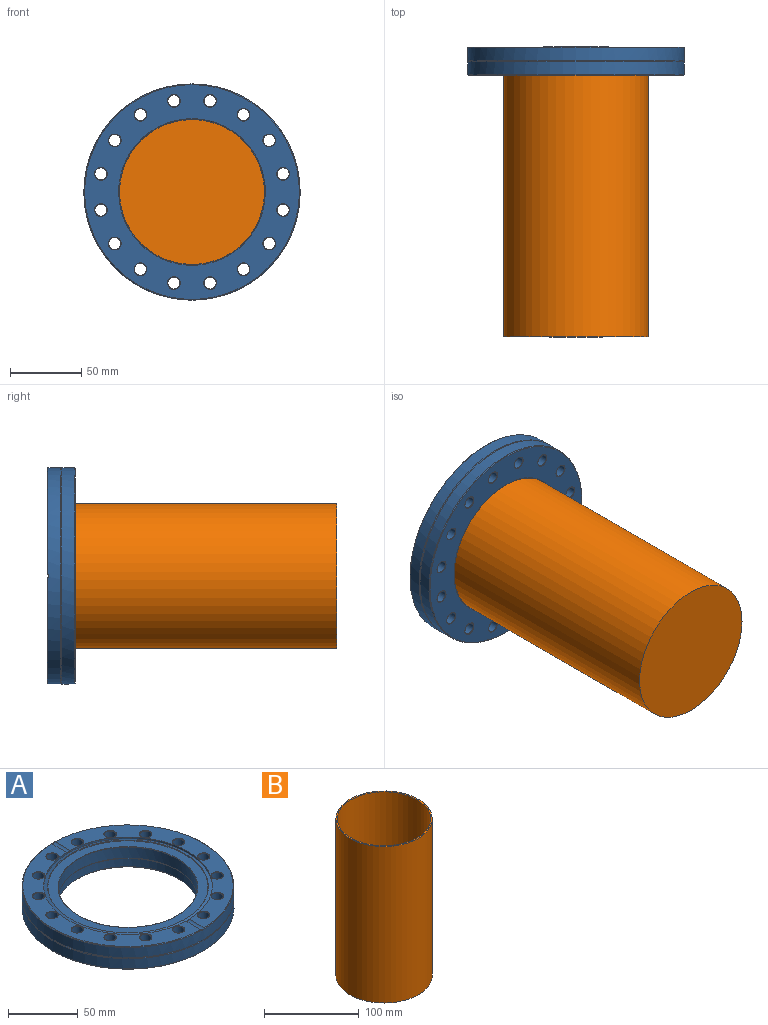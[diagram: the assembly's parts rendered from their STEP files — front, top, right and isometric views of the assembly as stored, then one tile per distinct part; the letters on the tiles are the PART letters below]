
ASSEMBLY  parts=2 mates=1
PART A: 71 faces, bbox 164.7x164.7x19.8 mm
  f0: cylinder r=75.82mm len=151.64mm, axis (0,0,1), area 4267.5mm2, adj f1,f2,f5,f11,f66
  f1: cylinder r=2.38mm len=15.51mm, axis (0,1,0), area 61.4mm2, adj f0,f2,f3,f4,f5,f6
  f2: cone r=75.82mm half-angle=45deg, axis (0,0,-1), area 168.5mm2, adj f0,f1,f3,f11
  f3: plane 150.58x73.54mm, normal (0,0,1), area 2637.6mm2, adj f1,f2,f4,f11,f12,f15,f18,f21
  f4: cylinder r=60.32mm len=120.65mm, axis (0,0,-1), area 644.5mm2, adj f1,f3,f6,f11,f68
  f5: cone r=75.82mm half-angle=45deg, axis (0,0,-1), area 168.5mm2, adj f0,f1,f6,f11
  f6: plane 150.58x73.54mm, normal (0,0,1), area 2637.6mm2, adj f1,f4,f5,f11,f36,f39,f42,f45
  f7: cylinder r=75.82mm len=151.64mm, axis (0,0,1), area 4267.5mm2, adj f63,f66
  f8: plane 150.62x150.62mm, normal (0,0,-1), area 8502.5mm2, adj f13,f16,f19,f22,f25,f28,f31,f34
  f9: cylinder r=50.93mm len=101.85mm, axis (0,0,-1), area 2273.2mm2, adj f60,f65
  f10: cylinder r=49.78mm len=99.57mm, axis (0,0,1), area 2963.5mm2, adj f61,f62
  f11: cylinder r=2.38mm len=15.51mm, axis (0,-1,0), area 61.4mm2, adj f0,f2,f3,f4,f5,f6
  f12: cone r=4.47mm half-angle=45deg, axis (0,0,1), area 9.8mm2, adj f3,f14
  f13: cone r=4.22mm half-angle=45deg, axis (0,0,-1), area 9.8mm2, adj f8,f14
  f14: cylinder r=4.22mm len=19.3mm, axis (0,0,1), area 511.4mm2, adj f12,f13
  f15: cone r=4.47mm half-angle=45deg, axis (0,0,1), area 9.8mm2, adj f3,f17
  f16: cone r=4.22mm half-angle=45deg, axis (0,0,-1), area 9.8mm2, adj f8,f17
  f17: cylinder r=4.22mm len=19.3mm, axis (0,0,1), area 511.4mm2, adj f15,f16
  f18: cone r=4.47mm half-angle=45deg, axis (0,0,1), area 9.8mm2, adj f3,f20
  f19: cone r=4.22mm half-angle=45deg, axis (0,0,-1), area 9.8mm2, adj f8,f20
  f20: cylinder r=4.22mm len=19.3mm, axis (0,0,1), area 511.4mm2, adj f18,f19
  f21: cone r=4.47mm half-angle=45deg, axis (0,0,1), area 9.8mm2, adj f3,f23
  f22: cone r=4.22mm half-angle=45deg, axis (0,0,-1), area 9.8mm2, adj f8,f23
  f23: cylinder r=4.22mm len=19.3mm, axis (0,0,1), area 511.4mm2, adj f21,f22
  f24: cone r=4.47mm half-angle=45deg, axis (0,0,1), area 9.8mm2, adj f3,f26
  f25: cone r=4.22mm half-angle=45deg, axis (0,0,-1), area 9.8mm2, adj f8,f26
  f26: cylinder r=4.22mm len=19.3mm, axis (0,0,1), area 511.4mm2, adj f24,f25
  f27: cone r=4.47mm half-angle=45deg, axis (0,0,1), area 9.8mm2, adj f3,f29
  f28: cone r=4.22mm half-angle=45deg, axis (0,0,-1), area 9.8mm2, adj f8,f29
  f29: cylinder r=4.22mm len=19.3mm, axis (0,0,1), area 511.4mm2, adj f27,f28
  f30: cone r=4.47mm half-angle=45deg, axis (0,0,1), area 9.8mm2, adj f3,f32
  f31: cone r=4.22mm half-angle=45deg, axis (0,0,-1), area 9.8mm2, adj f8,f32
  f32: cylinder r=4.22mm len=19.3mm, axis (0,0,1), area 511.4mm2, adj f30,f31
  f33: cone r=4.47mm half-angle=45deg, axis (0,0,1), area 9.8mm2, adj f3,f35
  f34: cone r=4.22mm half-angle=45deg, axis (0,0,-1), area 9.8mm2, adj f8,f35
  f35: cylinder r=4.22mm len=19.3mm, axis (0,0,1), area 511.4mm2, adj f33,f34
  f36: cone r=4.47mm half-angle=45deg, axis (0,0,1), area 9.8mm2, adj f6,f38
  f37: cone r=4.22mm half-angle=45deg, axis (0,0,-1), area 9.8mm2, adj f8,f38
  f38: cylinder r=4.22mm len=19.3mm, axis (0,0,1), area 511.4mm2, adj f36,f37
  f39: cone r=4.47mm half-angle=45deg, axis (0,0,1), area 9.8mm2, adj f6,f41
  f40: cone r=4.22mm half-angle=45deg, axis (0,0,-1), area 9.8mm2, adj f8,f41
  f41: cylinder r=4.22mm len=19.3mm, axis (0,0,1), area 511.4mm2, adj f39,f40
  f42: cone r=4.47mm half-angle=45deg, axis (0,0,1), area 9.8mm2, adj f6,f44
  f43: cone r=4.22mm half-angle=45deg, axis (0,0,-1), area 9.8mm2, adj f8,f44
  f44: cylinder r=4.22mm len=19.3mm, axis (0,0,1), area 511.4mm2, adj f42,f43
  f45: cone r=4.47mm half-angle=45deg, axis (0,0,1), area 9.8mm2, adj f6,f47
  f46: cone r=4.22mm half-angle=45deg, axis (0,0,-1), area 9.8mm2, adj f8,f47
  f47: cylinder r=4.22mm len=19.3mm, axis (0,0,1), area 511.4mm2, adj f45,f46
  f48: cone r=4.47mm half-angle=45deg, axis (0,0,1), area 9.8mm2, adj f6,f50
  f49: cone r=4.22mm half-angle=45deg, axis (0,0,-1), area 9.8mm2, adj f8,f50
  f50: cylinder r=4.22mm len=19.3mm, axis (0,0,1), area 511.4mm2, adj f48,f49
  f51: cone r=4.47mm half-angle=45deg, axis (0,0,1), area 9.8mm2, adj f6,f53
  f52: cone r=4.22mm half-angle=45deg, axis (0,0,-1), area 9.8mm2, adj f8,f53
  f53: cylinder r=4.22mm len=19.3mm, axis (0,0,1), area 511.4mm2, adj f51,f52
  f54: cone r=4.47mm half-angle=45deg, axis (0,0,1), area 9.8mm2, adj f6,f56
  f55: cone r=4.22mm half-angle=45deg, axis (0,0,-1), area 9.8mm2, adj f8,f56
  f56: cylinder r=4.22mm len=19.3mm, axis (0,0,1), area 511.4mm2, adj f54,f55
  f57: cone r=4.47mm half-angle=45deg, axis (0,0,1), area 9.8mm2, adj f6,f59
  f58: cone r=4.22mm half-angle=45deg, axis (0,0,-1), area 9.8mm2, adj f8,f59
  f59: cylinder r=4.22mm len=19.3mm, axis (0,0,1), area 511.4mm2, adj f57,f58
  f60: torus R=51.44mm, axis (0,0,-1), area 256.3mm2, adj f8,f9
  f61: torus R=49.99mm, axis (0,0,1), area 100mm2, adj f10,f70
  f62: torus R=50.04mm, axis (0,0,-1), area 125mm2, adj f10,f69
  f63: cone r=75.31mm half-angle=45deg, axis (0,0,1), area 341.1mm2, adj f7,f8
  f64: torus R=50.93mm, axis (0,0,1), area 261mm2, adj f65,f70
  f65: cone r=50.93mm half-angle=32deg, axis (0,0,1), area 195.7mm2, adj f9,f64
  f66: torus R=76.07mm, axis (0,0,1), area 505.7mm2, adj f0,f7
  f67: cone r=57.47mm half-angle=20deg, axis (0,0,1), area 194.9mm2, adj f68,f69
  f68: cone r=60.32mm half-angle=70deg, axis (0,0,-1), area 1125.3mm2, adj f4,f67
  f69: plane 114.57x114.57mm, normal (0,0,1), area 2442.6mm2, adj f62,f67
  f70: plane 101.85x101.85mm, normal (0,0,-1), area 297.9mm2, adj f61,f64
PART B: 5 faces, bbox 101.6x101.6x202 mm
  f0: cylinder r=49.3mm len=200mm, axis (0,0,1), area 61952.2mm2, adj f2,f3
  f1: cylinder r=50.8mm len=202mm, axis (0,0,1), area 64475.5mm2, adj f2,f4
  f2: plane 101.6x101.6mm, normal (0,0,1), area 471.7mm2, adj f0,f1
  f3: plane 98.6x98.6mm, normal (0,0,1), area 7635.6mm2, adj f0
  f4: plane 101.6x101.6mm, normal (0,0,-1), area 8107.3mm2, adj f1
PLACE A rot(axis=(-0.58,0.58,0.58),120deg) t=(-0.83,9.91,-4.36)mm
PLACE B rot(axis=(-1,0,0),90deg) t=(-0.83,18.64,-4.36)mm
MATE parallel B.f1 <-> A.f4  axis (0,1,0) through (-0.83,18.64,-4.36)mm
